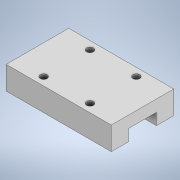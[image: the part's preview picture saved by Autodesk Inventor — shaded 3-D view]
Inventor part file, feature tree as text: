
AUTODESK INVENTOR PART (.ipt)
format: ipt  version: 2021 (Build 250183000, 183)  size: 117,248 bytes
history: native  units: mm
features: extrude x2, sketch x2
ambient origin geometry x8: Origin, YZ Plane, XZ Plane, XY Plane, X Axis, Y Axis, Z Axis, Center Point
bodies: Solid1 (feature_tree)
feature tree (4):
  extrude  "Extrusion1"  Depth=10.0mm
  extrude  "Extrusion2"  Depth=5.0mm
  sketch  "Sketch1"  dims[d0=27.0mm d1=10.0mm]
  sketch  "Sketch2"  dims[d2=12.0mm d3=5.0mm d4=7.5mm d5=45.4mm d6=0.0mm d7=20.0mm d8=3.0mm d9=3.0mm d10=3.5mm d11=12.7mm d12=45.4mm d13=0.0mm]
